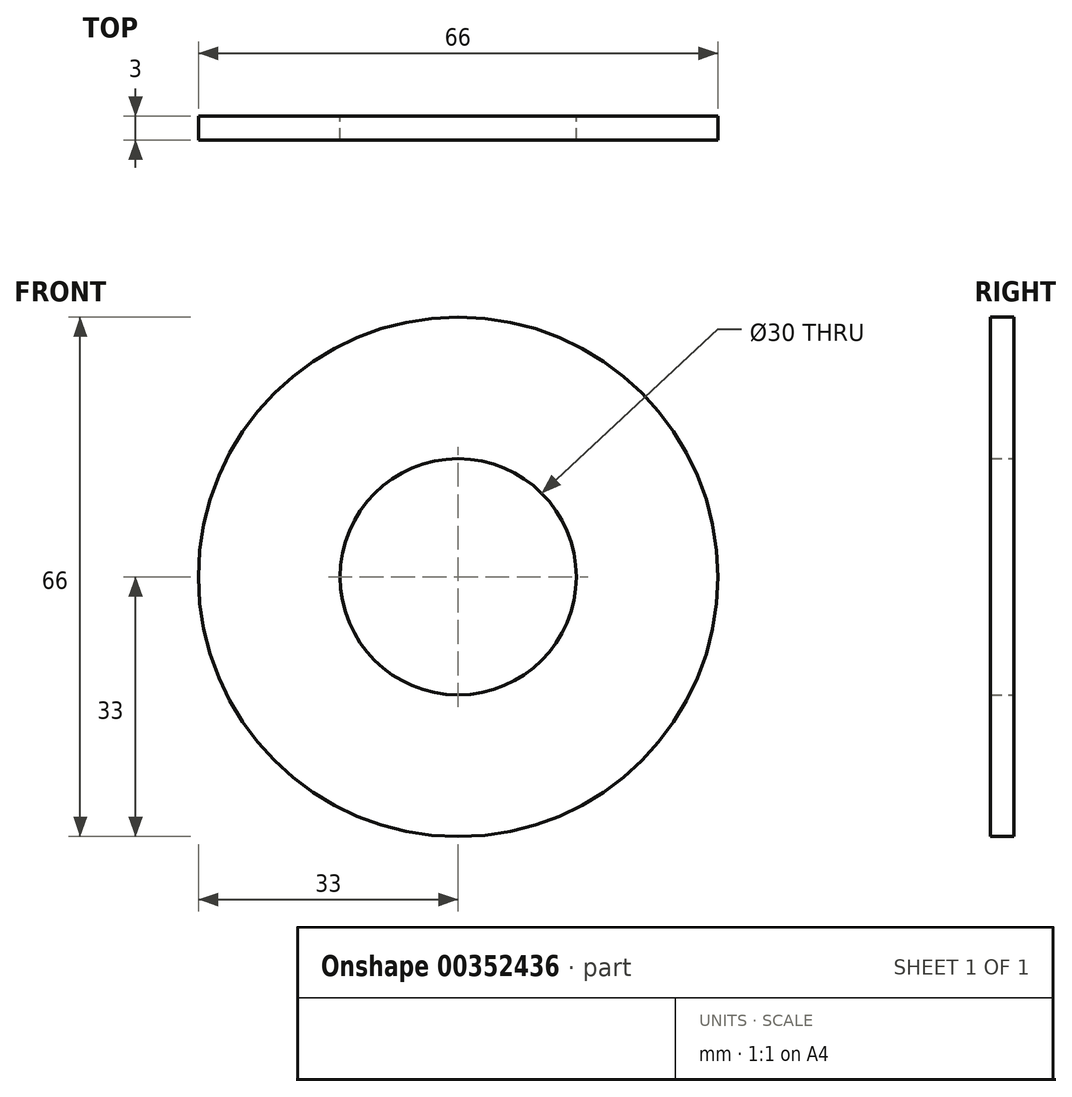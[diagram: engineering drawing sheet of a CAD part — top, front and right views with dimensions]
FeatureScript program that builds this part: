
annotation { "Feature Type Name" : "Feature", "Feature Type Description" : "" }
export const myFeature = defineFeature(function(context is Context, id is Id, definition is map)
    precondition{}
    {
        {
            var Q0;
            Q0=qCreatedBy(makeId("Front.planeOp"),FACE);
            var sketch = newSketch(context, id + "F0", { "sketchPlane" : qUnion([Q0])});
            skCircle(sketch, "E0", {"center": v(0, 0) * mm, "radius": 15 * mm});
            skCircle(sketch, "E1", {"center": v(0, 0) * mm, "radius": 33 * mm});
            skSolve(sketch);
        }
        {
            var Q0;
            Q0 = qSketchRegion(id + "F0", true);
            extrude(context, id + "F1", {"entities" : qUnion([Q0]), "depth" : 3 * mm, "symmetric" : true});
        }
    });
